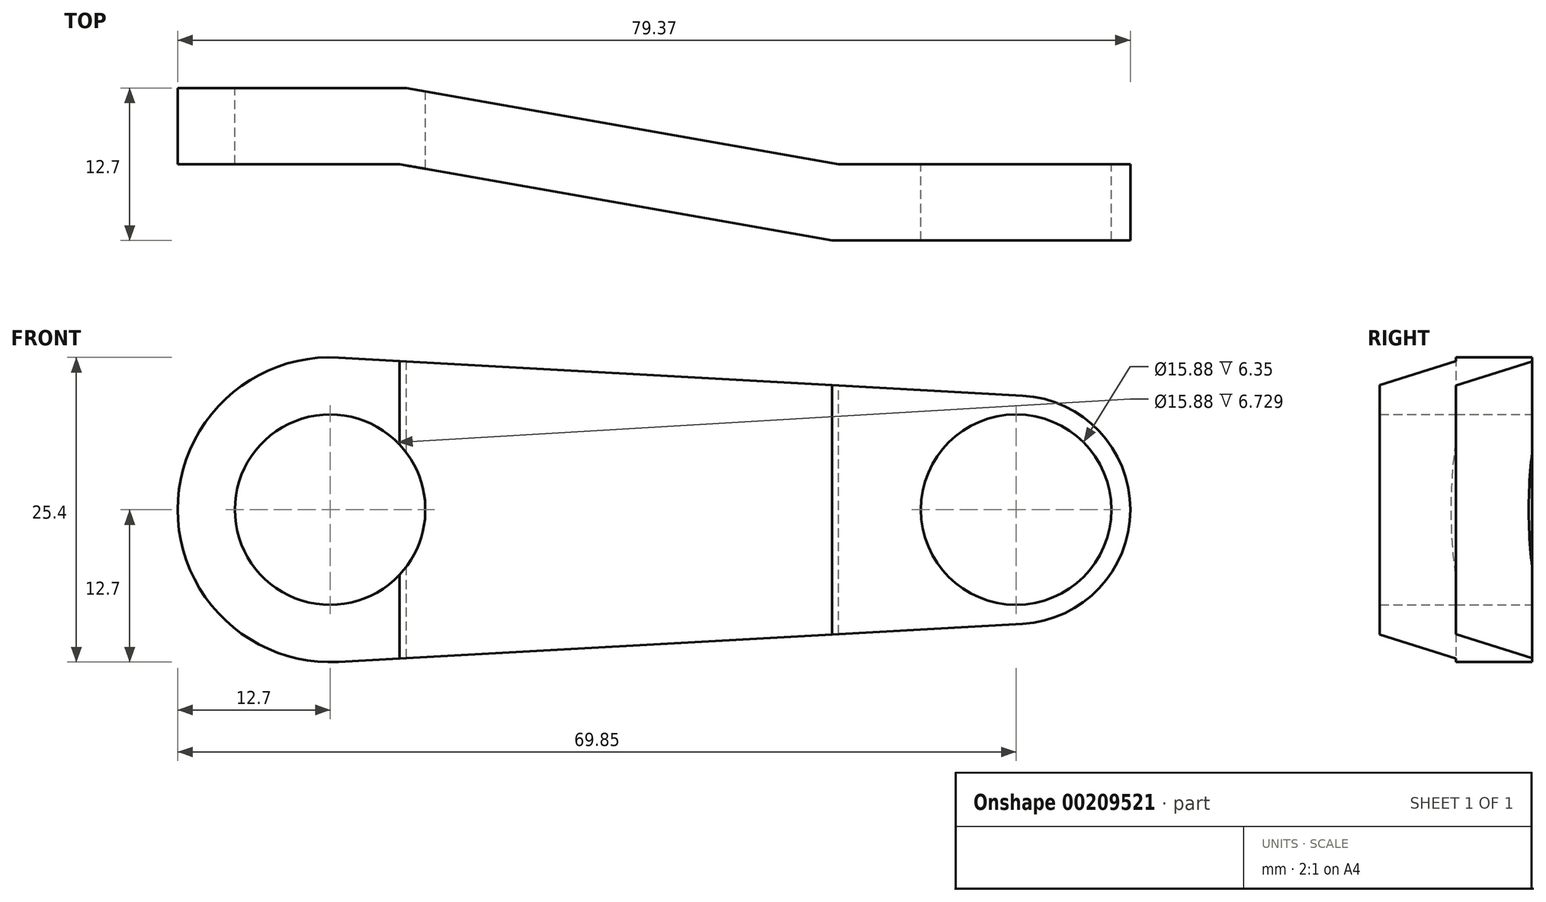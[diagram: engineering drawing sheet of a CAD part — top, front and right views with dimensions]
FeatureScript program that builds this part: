
annotation { "Feature Type Name" : "Feature", "Feature Type Description" : "" }
export const myFeature = defineFeature(function(context is Context, id is Id, definition is map)
    precondition{}
    {
        {
            var Q0;
            Q0=qCreatedBy(makeId("Front.planeOp"),FACE);
            var sketch = newSketch(context, id + "F0", { "sketchPlane" : qUnion([Q0])});
            skCircle(sketch, "E0", {"center": v(0, 0) * mm, "radius": 12.7 * mm});
            skCircle(sketch, "E1", {"center": v(57.15, 0) * mm, "radius": 9.53 * mm});
            skLineSegment(sketch, "E2", {"start": v(0.7, 12.68) * mm, "end": v(57.68, 9.51) * mm});
            skLineSegment(sketch, "E3", {"start": v(0.7, -12.68) * mm, "end": v(57.68, -9.51) * mm});
            skCircle(sketch, "E4", {"center": v(0, 0) * mm, "radius": 7.94 * mm});
            skCircle(sketch, "E5", {"center": v(57.15, 0) * mm, "radius": 7.94 * mm});
            skSolve(sketch);
        }
        {
            var Q0;
            Q0=qSketchRegion(id+"F0",true);
            extrude(context, id + "F1", {"entities" : qUnion([Q0]), "depth" : 19.05 * mm});
        }
        {
            var Q0;
            Q0=qCreatedBy(makeId("Top.planeOp"),FACE);
            var sketch = newSketch(context, id + "F2", { "sketchPlane" : qUnion([Q0])});
            skLineSegment(sketch, "E6", {"start": v(-12.7, 0) * mm, "end": v(6.35, 0) * mm});
            skLineSegment(sketch, "E7", {"start": v(6.35, 0) * mm, "end": v(42.36, -6.35) * mm});
            skLineSegment(sketch, "E8", {"start": v(42.36, -6.35) * mm, "end": v(66.68, -6.35) * mm});
            skLineSegment(sketch, "E9.0", {"start": v(41.8, -12.7) * mm, "end": v(66.68, -12.7) * mm});
            skLineSegment(sketch, "E9.1", {"start": v(5.8, -6.35) * mm, "end": v(41.8, -12.7) * mm});
            skLineSegment(sketch, "E9.2", {"start": v(-12.7, -6.35) * mm, "end": v(5.8, -6.35) * mm});
            skLineSegment(sketch, "E10", {"start": v(-12.7, -6.35) * mm, "end": v(-12.7, 0) * mm});
            skLineSegment(sketch, "E11", {"start": v(66.68, -12.7) * mm, "end": v(66.68, -6.35) * mm});
            skLineSegment(sketch, "E12", {"start": v(66.68, 0) * mm, "end": v(66.68, -19.05) * mm});
            skLineSegment(sketch, "E13", {"start": v(-12.7, -19.05) * mm, "end": v(-12.7, 0) * mm});
            skSolve(sketch);
        }
        {
            var Q0;
            Q0=qSketchRegion(id+"F2",true);
            extrude(context, id + "F3", {"entities" : qUnion([Q0]), "operationType" : NewBodyOperationType.INTERSECT, "endBound" : BoundingType.SYMMETRIC, "oppositeDirection" : true, "depth" : 25.4 * mm});
        }
    });
